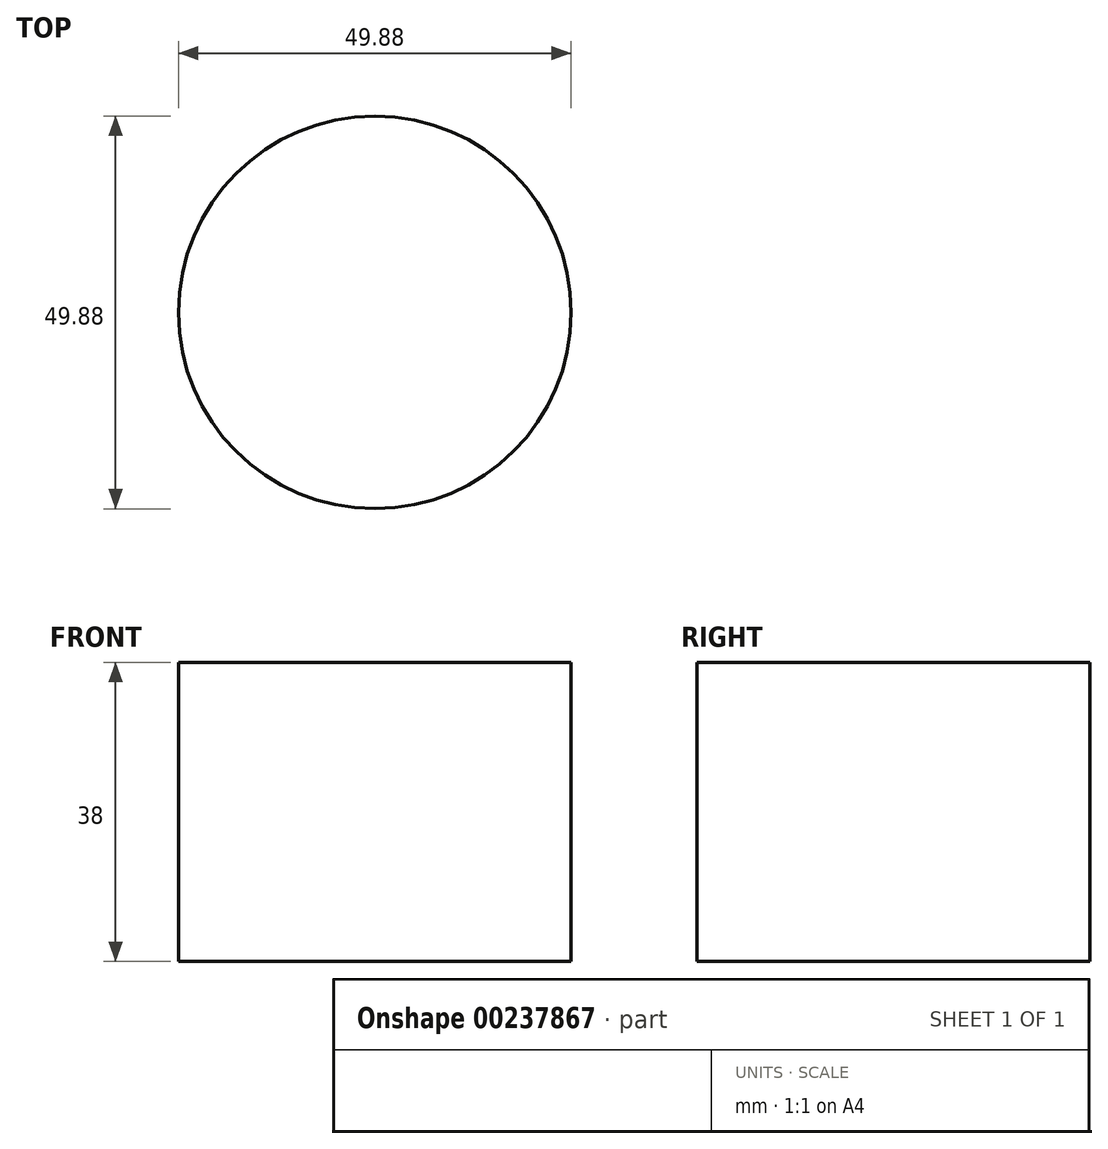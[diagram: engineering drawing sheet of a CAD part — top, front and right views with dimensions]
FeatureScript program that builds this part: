
annotation { "Feature Type Name" : "Feature", "Feature Type Description" : "" }
export const myFeature = defineFeature(function(context is Context, id is Id, definition is map)
    precondition{}
    {
        {
            var Q0;
            Q0=qCreatedBy(makeId("Top.planeOp"),FACE);
            var sketch = newSketch(context, id + "F0", { "sketchPlane" : qUnion([Q0])});
            skCircle(sketch, "E0", {"center": v(0, 0) * mm, "radius": 24.94 * mm});
            skSolve(sketch);
        }
        {
            var Q0;
            Q0 = qSketchRegion(id + "F0", true);
            extrude(context, id + "F1", {"entities" : qUnion([Q0]), "depth" : 38 * mm});
        }
    });
